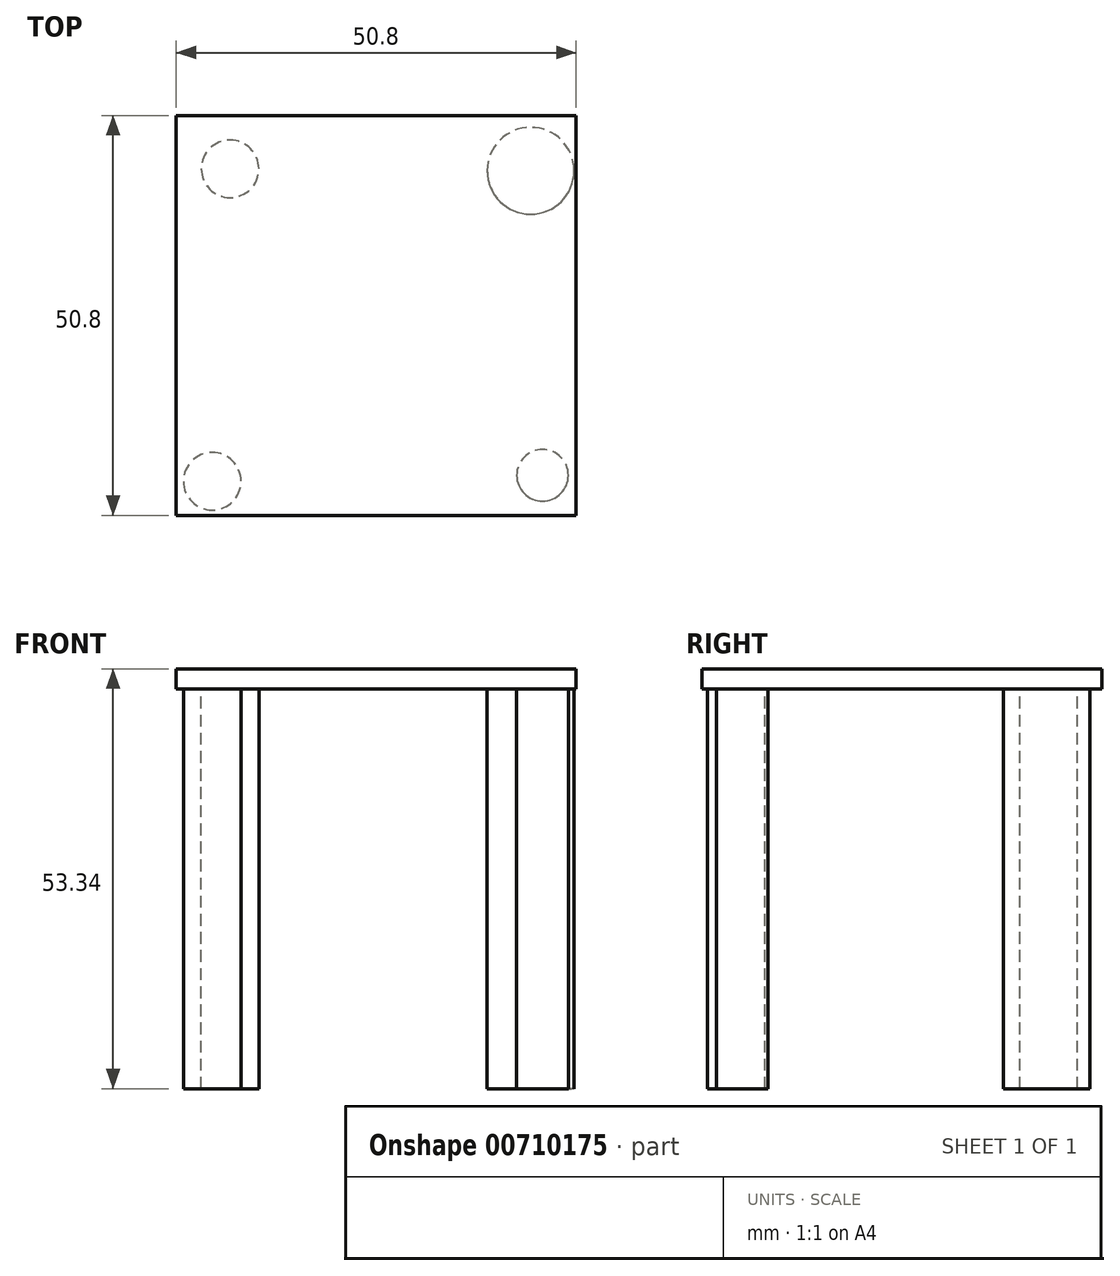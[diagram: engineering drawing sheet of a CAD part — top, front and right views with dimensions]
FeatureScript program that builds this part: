
annotation { "Feature Type Name" : "Feature", "Feature Type Description" : "" }
export const myFeature = defineFeature(function(context is Context, id is Id, definition is map)
    precondition{}
    {
        {
            var Q0;
            Q0=qCreatedBy(makeId("Front.planeOp"),FACE);
            var sketch = newSketch(context, id + "F0", { "sketchPlane" : qUnion([Q0])});
            skLineSegment(sketch, "E0.bottom", {"start": v(-1.44, 0.26) * mm, "end": v(49.36, 0.26) * mm});
            skLineSegment(sketch, "E0.top", {"start": v(-1.44, -2.28) * mm, "end": v(49.36, -2.28) * mm});
            skLineSegment(sketch, "E0.left", {"start": v(-1.44, 0.26) * mm, "end": v(-1.44, -2.28) * mm});
            skLineSegment(sketch, "E0.right", {"start": v(49.36, 0.26) * mm, "end": v(49.36, -2.28) * mm});
            skSolve(sketch);
        }
        {
            var Q0;
            Q0 = qSketchRegion(id + "F0", true);
            extrude(context, id + "F1", {"entities" : qUnion([Q0]), "depth" : 50.8 * mm, "offsetDistance" : 25.4 * mm});
        }
        {
            var Q0;
            Q0=makeQuery(id+"F1.opExtrude","SWEPT_FACE",FACE,{"disambiguationData":[OSD([sQuery(id+"F0.wireOp",EDGE,"E0.top")])]});
            var sketch = newSketch(context, id + "F2", { "sketchPlane" : qUnion([Q0])});
            skCircle(sketch, "E1", {"center": v(3.14, 46.47) * mm, "radius": 3.66 * mm});
            skCircle(sketch, "E2", {"center": v(45.1, 45.72) * mm, "radius": 3.28 * mm});
            skCircle(sketch, "E3", {"center": v(5.4, 6.78) * mm, "radius": 3.66 * mm});
            skCircle(sketch, "E4", {"center": v(43.58, 7.03) * mm, "radius": 5.52 * mm});
            skSolve(sketch);
        }
        {
            var Q0;
            Q0 = qSketchRegion(id + "F2", true);
            extrude(context, id + "F3", {"entities" : qUnion([Q0]), "operationType" : NewBodyOperationType.ADD, "depth" : 50.8 * mm, "offsetDistance" : 25.4 * mm});
        }
    });
